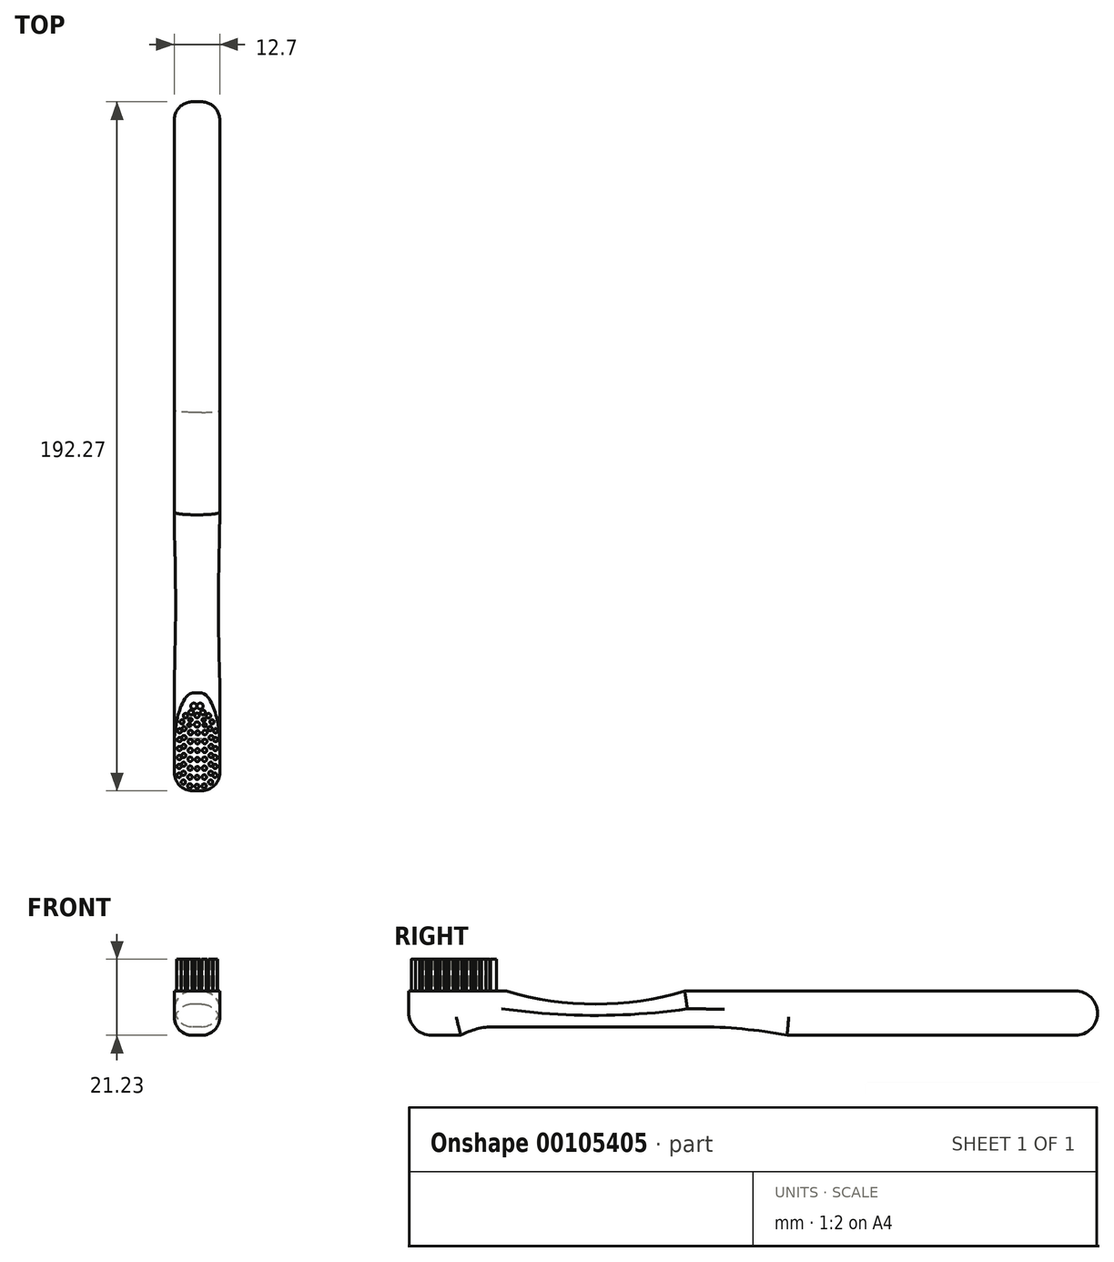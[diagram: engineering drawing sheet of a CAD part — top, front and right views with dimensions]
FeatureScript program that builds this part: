
annotation { "Feature Type Name" : "Feature", "Feature Type Description" : "" }
export const myFeature = defineFeature(function(context is Context, id is Id, definition is map)
    precondition{}
    {
        {
            var Q0;
            Q0=qCreatedBy(makeId("Right.planeOp"),FACE);
            var sketch = newSketch(context, id + "F0", { "sketchPlane" : qUnion([Q0])});
            skLineSegment(sketch, "E0.bottom", {"start": v(93.05, 6.17) * mm, "end": v(-16.01, 6.17) * mm});
            skLineSegment(sketch, "E0.top", {"start": v(93.05, -6.17) * mm, "end": v(12.55, -6.17) * mm});
            skLineSegment(sketch, "E0.right", {"start": v(-93.05, 6.17) * mm, "end": v(-93.05, 0.18) * mm});
            skPoint(sketch, "E0.middle", {"position": v(0, 0) * mm});
            skArc(sketch, "E1", {"start": v(93.05, -6.17) * mm, "mid": v(99.22, 0) * mm, "end": v(93.05, 6.17) * mm});
            skArc(sketch, "E2", {"start": v(-65.78, 6.17) * mm, "mid": v(-40.9, 2.55) * mm, "end": v(-16.01, 6.17) * mm});
            skLineSegment(sketch, "E3.bottom", {"start": v(-12.55, -3.79) * mm, "end": v(-69.25, -3.79) * mm});
            skPoint(sketch, "E3.middle", {"position": v(-40.9, -6.17) * mm});
            skPoint(sketch, "E3.middle.positionSnap0", {"position": v(-40.9, 2.55) * mm});
            skPoint(sketch, "E3.centerSnap0", {"position": v(-40.9, 2.55) * mm});
            skArc(sketch, "E4", {"start": v(-69.25, -3.79) * mm, "mid": v(-74.05, -4.4) * mm, "end": v(-78.55, -6.17) * mm});
            skArc(sketch, "E5", {"start": v(12.55, -6.17) * mm, "mid": v(0.06, -4.38) * mm, "end": v(-12.55, -3.79) * mm});
            skPoint(sketch, "E6.visualSharp", {"position": v(-93.05, -6.17) * mm});
            skArc(sketch, "E6.filletArc", {"start": v(-93.05, 0.18) * mm, "mid": v(-91.19, -4.3) * mm, "end": v(-86.7, -6.17) * mm});
            skPoint(sketch, "E7.orphan", {"position": v(-69.25, -8.55) * mm});
            skPoint(sketch, "E3.left.end.orphan", {"position": v(-12.55, -8.55) * mm});
            skLineSegment(sketch, "E8.trimOffspring", {"start": v(-78.55, -6.17) * mm, "end": v(-86.7, -6.17) * mm});
            skLineSegment(sketch, "E9.trimOffspring", {"start": v(-65.78, 6.17) * mm, "end": v(-93.05, 6.17) * mm});
            skSolve(sketch);
        }
        {
            var Q0;
            Q0=makeQuery(id+"F0.imprint","IMPRINT",FACE,{"disambiguationData":[TD([[makeQuery(id+"F0.imprint","IMPRINT",EDGE,{"derivedFrom":sQuery(id+"F0.wireOp",EDGE,"E0.bottom")}),1.0]])]});
            extrude(context, id + "F1", {"entities" : qUnion([Q0]), "endBound" : BoundingType.SYMMETRIC, "depth" : 12.7 * mm});
        }
        {
            var Q0;
            Q0=makeQuery(id+"F1.opExtrude","SWEPT_FACE",FACE,{"disambiguationData":[OSD([sQuery(id+"F0.wireOp",EDGE,"E9.trimOffspring")])]});
            var sketch = newSketch(context, id + "F2", { "sketchPlane" : qUnion([Q0])});
            skLineSegment(sketch, "E10", {"start": v(0, -65.78) * mm, "end": v(0, -93.05) * mm});
            skCircle(sketch, "E11", {"center": v(0, -91.8) * mm, "radius": 0.58 * mm});
            skCircle(sketch, "E12", {"center": v(2, -91.71) * mm, "radius": 0.63 * mm});
            skCircle(sketch, "E13", {"center": v(3.8, -90.63) * mm, "radius": 0.59 * mm});
            skCircle(sketch, "E14", {"center": v(5.02, -88.72) * mm, "radius": 0.6 * mm});
            skCircle(sketch, "E15.MirrorC", {"center": v(-3.8, -90.63) * mm, "radius": 0.59 * mm});
            skCircle(sketch, "E16.MirrorC", {"center": v(-5.02, -88.72) * mm, "radius": 0.6 * mm});
            skCircle(sketch, "E17.MirrorC", {"center": v(-2, -91.71) * mm, "radius": 0.63 * mm});
            skCircle(sketch, "E18.0.1.0", {"center": v(-3.78, -88.14) * mm, "radius": 0.59 * mm});
            skCircle(sketch, "E18.0.1.1", {"center": v(2.02, -89.22) * mm, "radius": 0.63 * mm});
            skCircle(sketch, "E18.0.1.2", {"center": v(0.03, -89.31) * mm, "radius": 0.58 * mm});
            skCircle(sketch, "E18.0.1.3", {"center": v(3.84, -88.14) * mm, "radius": 0.59 * mm});
            skCircle(sketch, "E18.0.1.4", {"center": v(5.05, -86.24) * mm, "radius": 0.6 * mm});
            skCircle(sketch, "E18.0.1.5", {"center": v(-5, -86.24) * mm, "radius": 0.6 * mm});
            skCircle(sketch, "E18.0.1.6", {"center": v(-1.96, -89.22) * mm, "radius": 0.63 * mm});
            skCircle(sketch, "E18.0.1.7", {"center": v(0.03, -89.31) * mm, "radius": 0.58 * mm});
            skCircle(sketch, "E18.0.2.0", {"center": v(-3.75, -85.66) * mm, "radius": 0.59 * mm});
            skCircle(sketch, "E18.0.2.1", {"center": v(2.05, -86.74) * mm, "radius": 0.63 * mm});
            skCircle(sketch, "E18.0.2.2", {"center": v(0.06, -86.83) * mm, "radius": 0.58 * mm});
            skCircle(sketch, "E18.0.2.3", {"center": v(3.87, -85.66) * mm, "radius": 0.59 * mm});
            skCircle(sketch, "E18.0.2.4", {"center": v(5.08, -83.75) * mm, "radius": 0.6 * mm});
            skCircle(sketch, "E18.0.2.5", {"center": v(-4.96, -83.75) * mm, "radius": 0.6 * mm});
            skCircle(sketch, "E18.0.2.6", {"center": v(-1.93, -86.74) * mm, "radius": 0.63 * mm});
            skCircle(sketch, "E18.0.2.7", {"center": v(0.06, -86.83) * mm, "radius": 0.58 * mm});
            skCircle(sketch, "E18.0.3.0", {"center": v(-3.72, -83.17) * mm, "radius": 0.59 * mm});
            skCircle(sketch, "E18.0.3.1", {"center": v(2.08, -84.25) * mm, "radius": 0.63 * mm});
            skCircle(sketch, "E18.0.3.2", {"center": v(0.1, -84.34) * mm, "radius": 0.58 * mm});
            skCircle(sketch, "E18.0.3.3", {"center": v(3.9, -83.17) * mm, "radius": 0.59 * mm});
            skCircle(sketch, "E18.0.3.4", {"center": v(5.11, -81.27) * mm, "radius": 0.6 * mm});
            skCircle(sketch, "E18.0.3.5", {"center": v(-4.93, -81.27) * mm, "radius": 0.6 * mm});
            skCircle(sketch, "E18.0.3.6", {"center": v(-1.9, -84.25) * mm, "radius": 0.63 * mm});
            skCircle(sketch, "E18.0.3.7", {"center": v(0.1, -84.34) * mm, "radius": 0.58 * mm});
            skCircle(sketch, "E18.0.4.0", {"center": v(-3.69, -80.69) * mm, "radius": 0.59 * mm});
            skCircle(sketch, "E18.0.4.1", {"center": v(2.11, -81.77) * mm, "radius": 0.63 * mm});
            skCircle(sketch, "E18.0.4.2", {"center": v(0.12, -81.86) * mm, "radius": 0.58 * mm});
            skCircle(sketch, "E18.0.4.3", {"center": v(3.93, -80.69) * mm, "radius": 0.59 * mm});
            skCircle(sketch, "E18.0.4.4", {"center": v(5.14, -78.78) * mm, "radius": 0.6 * mm});
            skCircle(sketch, "E18.0.4.5", {"center": v(-4.9, -78.78) * mm, "radius": 0.6 * mm});
            skCircle(sketch, "E18.0.4.6", {"center": v(-1.87, -81.77) * mm, "radius": 0.63 * mm});
            skCircle(sketch, "E18.0.4.7", {"center": v(0.12, -81.86) * mm, "radius": 0.58 * mm});
            skCircle(sketch, "E18.0.5.0", {"center": v(-3.66, -78.2) * mm, "radius": 0.59 * mm});
            skCircle(sketch, "E18.0.5.1", {"center": v(2.14, -79.28) * mm, "radius": 0.63 * mm});
            skCircle(sketch, "E18.0.5.2", {"center": v(0.15, -79.37) * mm, "radius": 0.58 * mm});
            skCircle(sketch, "E18.0.5.3", {"center": v(3.96, -78.2) * mm, "radius": 0.59 * mm});
            skCircle(sketch, "E18.0.5.4", {"center": v(5.18, -76.3) * mm, "radius": 0.6 * mm});
            skCircle(sketch, "E18.0.5.5", {"center": v(-4.87, -76.3) * mm, "radius": 0.6 * mm});
            skCircle(sketch, "E18.0.5.6", {"center": v(-1.84, -79.28) * mm, "radius": 0.63 * mm});
            skCircle(sketch, "E18.0.5.7", {"center": v(0.15, -79.37) * mm, "radius": 0.58 * mm});
            skCircle(sketch, "E18.0.6.0", {"center": v(-3.62, -75.72) * mm, "radius": 0.59 * mm});
            skCircle(sketch, "E18.0.6.1", {"center": v(2.17, -76.8) * mm, "radius": 0.63 * mm});
            skCircle(sketch, "E18.0.6.2", {"center": v(0.18, -76.89) * mm, "radius": 0.58 * mm});
            skCircle(sketch, "E18.0.6.6", {"center": v(-1.8, -76.8) * mm, "radius": 0.63 * mm});
            skCircle(sketch, "E18.0.6.7", {"center": v(0.18, -76.89) * mm, "radius": 0.58 * mm});
            skLineSegment(sketch, "E18.direction2", {"start": v(-3.8, -90.63) * mm, "end": v(-3.78, -88.14) * mm, "construction": true});
            skCircle(sketch, "E19", {"center": v(-4.19, -73.81) * mm, "radius": 0.59 * mm});
            skCircle(sketch, "E20", {"center": v(-3.23, -72.1) * mm, "radius": 0.62 * mm});
            skCircle(sketch, "E21", {"center": v(-1.64, -71.2) * mm, "radius": 0.69 * mm});
            skCircle(sketch, "E22", {"center": v(-1.85, -73.26) * mm, "radius": 0.48 * mm});
            skCircle(sketch, "E23", {"center": v(-2.13, -74.7) * mm, "radius": 0.49 * mm});
            skCircle(sketch, "E24", {"center": v(0, -74.57) * mm, "radius": 0.74 * mm});
            skCircle(sketch, "E25", {"center": v(0, -72.02) * mm, "radius": 0.65 * mm});
            skCircle(sketch, "E26", {"center": v(-0.89, -69.41) * mm, "radius": 0.84 * mm});
            skCircle(sketch, "E27.MirrorC", {"center": v(2.13, -74.7) * mm, "radius": 0.49 * mm});
            skCircle(sketch, "E28.MirrorC", {"center": v(4.19, -73.81) * mm, "radius": 0.59 * mm});
            skCircle(sketch, "E29.MirrorC", {"center": v(3.62, -75.72) * mm, "radius": 0.59 * mm});
            skCircle(sketch, "E30.MirrorC", {"center": v(1.85, -73.26) * mm, "radius": 0.48 * mm});
            skCircle(sketch, "E31.MirrorC", {"center": v(0.89, -69.41) * mm, "radius": 0.84 * mm});
            skCircle(sketch, "E32.MirrorC", {"center": v(3.23, -72.1) * mm, "radius": 0.62 * mm});
            skCircle(sketch, "E33.MirrorC", {"center": v(1.64, -71.2) * mm, "radius": 0.69 * mm});
            skSolve(sketch);
        }
        {
            var Q0;
            Q0=qSketchRegion(id+"F2",true);
            extrude(context, id + "F3", {"entities" : qUnion([Q0]), "operationType" : NewBodyOperationType.ADD, "depth" : 8.9 * mm});
        }
        {
            var Q0;
            Q0=makeQuery(id+"F1.opExtrude","CAP_EDGE",EDGE,{"disambiguationData":[OSD([sQuery(id+"F0.wireOp",EDGE,"E0.bottom")])],"isStart":true});
            var Q1;
            Q1=makeQuery(id+"F1.opExtrude","CAP_EDGE",EDGE,{"disambiguationData":[OSD([sQuery(id+"F0.wireOp",EDGE,"E2")])],"isStart":true});
            var Q2;
            Q2=makeQuery(id+"F1.opExtrude","CAP_EDGE",EDGE,{"disambiguationData":[OSD([sQuery(id+"F0.wireOp",EDGE,"E3.bottom")])],"isStart":true});
            var Q3;
            Q3=makeQuery(id+"F1.opExtrude","CAP_EDGE",EDGE,{"disambiguationData":[OSD([sQuery(id+"F0.wireOp",EDGE,"E5")])],"isStart":true});
            var Q4;
            Q4=makeQuery(id+"F1.opExtrude","CAP_EDGE",EDGE,{"disambiguationData":[OSD([sQuery(id+"F0.wireOp",EDGE,"E0.top")])],"isStart":true});
            var Q5;
            Q5=makeQuery(id+"F1.opExtrude","CAP_EDGE",EDGE,{"disambiguationData":[OSD([sQuery(id+"F0.wireOp",EDGE,"E0.top")])],"isStart":false});
            var Q6;
            Q6=makeQuery(id+"F1.opExtrude","CAP_EDGE",EDGE,{"disambiguationData":[OSD([sQuery(id+"F0.wireOp",EDGE,"E5")])],"isStart":false});
            var Q7;
            Q7=makeQuery(id+"F1.opExtrude","CAP_EDGE",EDGE,{"disambiguationData":[OSD([sQuery(id+"F0.wireOp",EDGE,"E3.bottom")])],"isStart":false});
            var Q8;
            Q8=makeQuery(id+"F1.opExtrude","CAP_EDGE",EDGE,{"disambiguationData":[OSD([sQuery(id+"F0.wireOp",EDGE,"E2")])],"isStart":false});
            var Q9;
            Q9=makeQuery(id+"F1.opExtrude","CAP_EDGE",EDGE,{"disambiguationData":[OSD([sQuery(id+"F0.wireOp",EDGE,"E6.filletArc")])],"isStart":false});
            var Q10;
            Q10=makeQuery(id+"F1.opExtrude","CAP_EDGE",EDGE,{"disambiguationData":[OSD([sQuery(id+"F0.wireOp",EDGE,"E6.filletArc")])],"isStart":true});
            fillet(context, id + "F4", {"entities" : qUnion([Q0, Q1, Q2, Q3, Q4, Q5, Q6, Q7, Q8, Q9, Q10]), "radius" : 5.08 * mm, "tangentPropagation" : true, "allowEdgeOverflow" : false});
        }
    });
